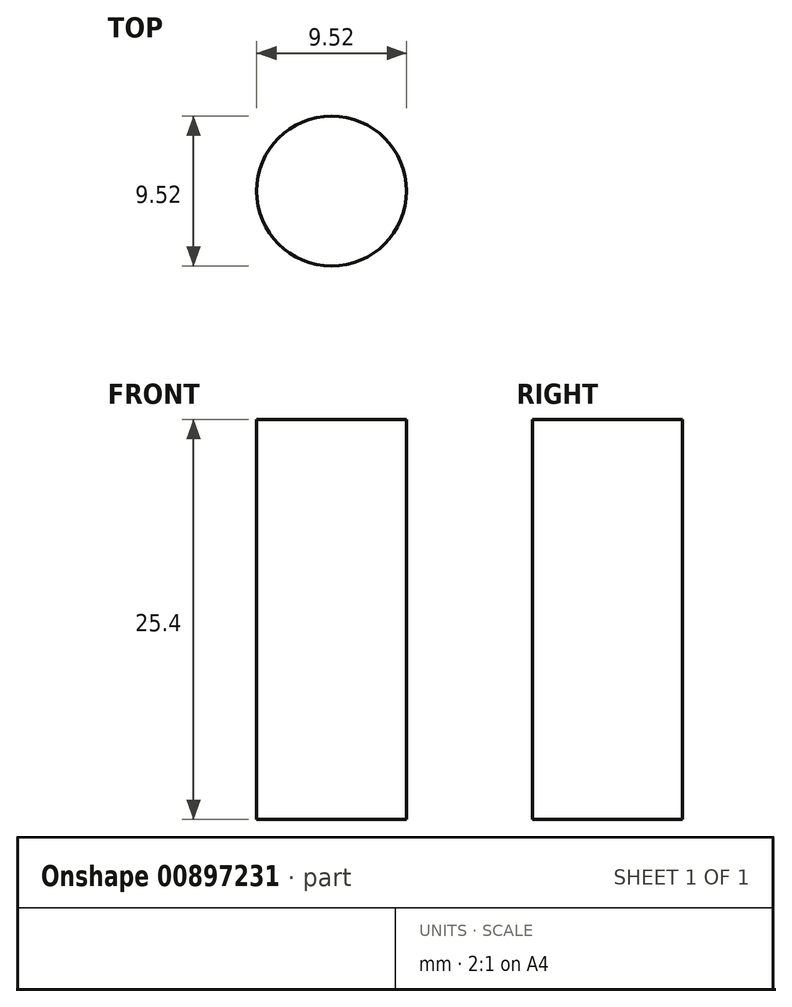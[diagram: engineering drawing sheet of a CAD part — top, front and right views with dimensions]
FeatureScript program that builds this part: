
annotation { "Feature Type Name" : "Feature", "Feature Type Description" : "" }
export const myFeature = defineFeature(function(context is Context, id is Id, definition is map)
    precondition{}
    {
        {
            var Q0;
            Q0=qCreatedBy(makeId("Top.planeOp"),FACE);
            var sketch = newSketch(context, id + "F0", { "sketchPlane" : qUnion([Q0])});
            skCircle(sketch, "E0", {"center": v(0, 0) * mm, "radius": 4.76 * mm});
            skSolve(sketch);
        }
        {
            var Q0;
            Q0 = qSketchRegion(id + "F0", true);
            extrude(context, id + "F1", {"entities" : qUnion([Q0]), "depth" : 25.4 * mm, "offsetDistance" : 25.4 * mm});
        }
    });
